# Revit family: DC_Holyoake_ReturnGrille_EC-125-FR_13
name_source: partatom
category: Air Terminals
revit_build: Autodesk Revit 2013 (Build: 20120221_2030(x64)
units: mm (PartAtom-declared; Revit-internal decimal feet)

## types (1)
- DC_Holyoake_ReturnGrille_EC-125-FR_13
    Default Elevation = 0 mm  [stored 0 ft]
    Description = Holyoake Exhaust and Return Grille EC-125-FR
    Engineering Data = http://www.productspec.net
    Exact Neck Height = 983 mm  [stored 3.22507 ft]
    Exact Neck Width = 683 mm  [stored 2.24081 ft]
    Filter Frame Height = 976 mm  [stored 3.2021 ft]
    Filter Frame Width = 676 mm
    Filter Height = 959.7 mm
    Filter Width = 659.7 mm
    Grille Depth = 45.5 mm  [stored 0.149278 ft]
    Grille Filter = Return Grille - Holyoake - Filter, Fabric
    Grille Frame = Return Grille - Holyoake - Frame, Aluminium
    Manufacturer = Holyoake Industries Ltd
    Max Flow = 200.0 L/s
    Min Flow = 20.0 L/s
    Model = EC-125-FR
    Nominal Height = 1000 mm  [stored 3.28084 ft]
    Nominal Width = 700 mm  [stored 2.29659 ft]
    Overall Height = 1031 mm  [stored 3.38255 ft]
    Overall Width = 731 mm  [stored 2.39829 ft]
    Removable Core = Return Grille - Holyoake - Removable Core, Aluminium
    Removable Core Width = 706.88 mm  [stored 2.31916 ft]
    Static Pressure Max = 160.00 Pa
    Static Pressure Min = 10.00 Pa
    Type Comments = Exhaust and Return Grille
    URL = http://www.productspec.net

note: [stored X ft] marks values corroborated as IEEE doubles in the binary element streams (Revit-internal decimal feet)

## geometry (parser evidence)
native form markers: Blend x10, Sweep x4
no freeform markers — native parametric forms only
